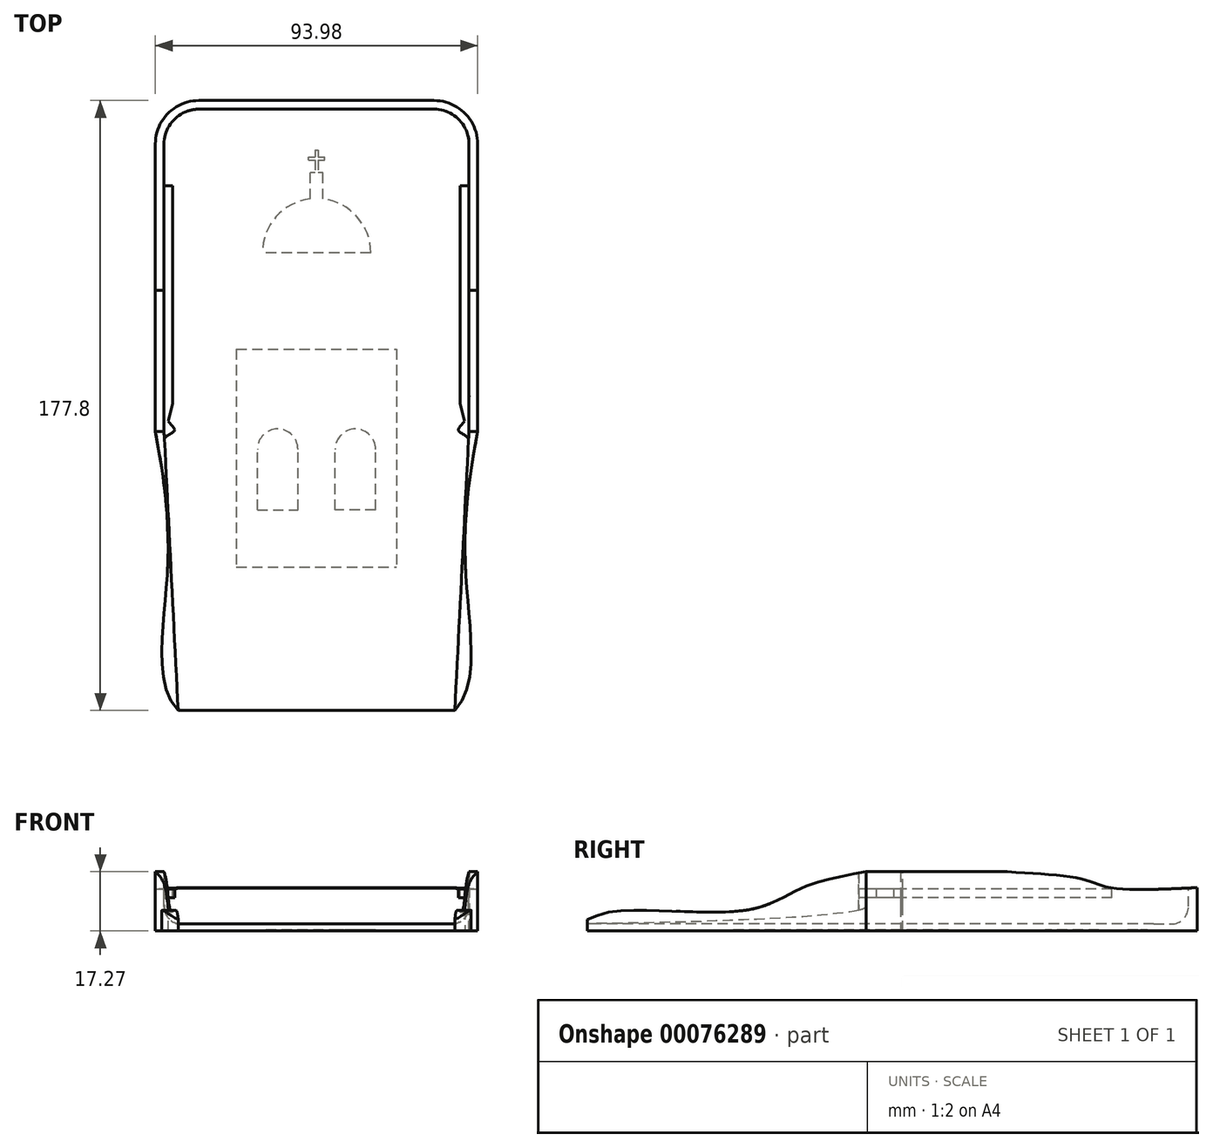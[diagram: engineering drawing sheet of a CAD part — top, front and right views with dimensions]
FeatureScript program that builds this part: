
annotation { "Feature Type Name" : "Feature", "Feature Type Description" : "" }
export const myFeature = defineFeature(function(context is Context, id is Id, definition is map)
    precondition{}
    {
        {
            var Q0;
            Q0=qCreatedBy(makeId("Top.planeOp"),FACE);
            var sketch = newSketch(context, id + "F0", { "sketchPlane" : qUnion([Q0])});
            skLineSegment(sketch, "E0.bottom", {"start": v(34.3, 88.9) * mm, "end": v(-34.3, 88.9) * mm});
            skLineSegment(sketch, "E0.top", {"start": v(46.99, -88.9) * mm, "end": v(-46.99, -88.9) * mm});
            skLineSegment(sketch, "E0.left", {"start": v(46.99, 76.2) * mm, "end": v(46.99, -88.9) * mm});
            skLineSegment(sketch, "E0.right", {"start": v(-47, 76.2) * mm, "end": v(-46.99, -88.9) * mm});
            skPoint(sketch, "E0.middle", {"position": v(0, 0) * mm});
            skPoint(sketch, "E1.visualSharp", {"position": v(-47, 88.9) * mm});
            skArc(sketch, "E1.filletArc", {"start": v(-34.3, 88.9) * mm, "mid": v(-43.27, 85.18) * mm, "end": v(-47, 76.2) * mm});
            skPoint(sketch, "E2.visualSharp", {"position": v(47, 88.9) * mm});
            skArc(sketch, "E2.filletArc", {"start": v(47, 76.2) * mm, "mid": v(43.27, 85.18) * mm, "end": v(34.3, 88.9) * mm});
            skLineSegment(sketch, "E3", {"start": v(0, -88.9) * mm, "end": v(-38.1, -88.9) * mm});
            skLineSegment(sketch, "E4", {"start": v(0, -88.9) * mm, "end": v(38.1, -88.9) * mm});
            skLineSegment(sketch, "E5", {"start": v(47, -88.9) * mm, "end": v(46.99, -7.62) * mm});
            skLineSegment(sketch, "E6.MirrorCS", {"start": v(-46.99, -88.9) * mm, "end": v(-47, -7.62) * mm});
            skPoint(sketch, "E7.1.internal.snap0", {"position": v(-46.99, -48.26) * mm});
            skFitSpline(sketch, "E7", {"points": [v(-46.99, -7.62) * mm, v(-43.45, -48.26) * mm, v(-40.33, -88.9) * mm, v(0, -95.06) * mm], "startDerivative": vector(20.85, -110.2) * mm, "endDerivative": vector(121.73, 3.89) * mm});
            skFitSpline(sketch, "E8.MirrorCS", {"points": [v(46.99, -7.62) * mm, v(43.45, -48.26) * mm, v(40.33, -88.9) * mm, v(0, -95.06) * mm], "startDerivative": vector(-20.85, -110.2) * mm, "endDerivative": vector(-121.73, 3.89) * mm});
            skLineSegment(sketch, "E9.bottom", {"start": v(-47, 66.55) * mm, "end": v(-44.45, 66.55) * mm});
            skLineSegment(sketch, "E9.left", {"start": v(-47, 66.55) * mm, "end": v(-46.99, -7.62) * mm});
            skLineSegment(sketch, "E10", {"start": v(53.05, 88.9) * mm, "end": v(-69.01, 88.9) * mm, "construction": true});
            skPoint(sketch, "E11.endSnap0", {"position": v(-46.99, 29.46) * mm});
            skLineSegment(sketch, "E12", {"start": v(-44.45, 66.55) * mm, "end": v(-44.45, 3.05) * mm});
            skLineSegment(sketch, "E13", {"start": v(-43.94, -2.03) * mm, "end": v(-43.94, -7.11) * mm});
            skPoint(sketch, "E14.1.internal.snap0", {"position": v(-43.94, -4.57) * mm});
            skLineSegment(sketch, "E15", {"start": v(0, 97.45) * mm, "end": v(0, -108.32) * mm, "construction": true});
            skLineSegment(sketch, "E16.MirrorCS", {"start": v(44.45, 66.55) * mm, "end": v(44.45, -2.03) * mm});
            skFitSpline(sketch, "E17.MirrorCS", {"points": [v(44.45, 3.05) * mm, v(42.16, -2.03) * mm], "startDerivative": vector(1.27, -5.08) * mm, "endDerivative": vector(1.27, -5.08) * mm});
            skFitSpline(sketch, "E18.MirrorCS", {"points": [v(42.16, -2.03) * mm, v(41, -4.57) * mm, v(42.16, -5.96) * mm, v(46.99, -7.62) * mm], "startDerivative": vector(-5.11, -7.46) * mm, "endDerivative": vector(3.51, -5.4) * mm});
            skSolve(sketch);
        }
        {
            var Q0;
            Q0=makeQuery(id+"F0.imprint","IMPRINT",FACE,{"disambiguationData":[TD([[makeQuery(id+"F0.imprint","IMPRINT",EDGE,{"derivedFrom":sQuery(id+"F0.wireOp",EDGE,"E0.bottom")}),1.0]])]});
            extrude(context, id + "F1", {"entities" : qUnion([Q0]), "depth" : 17.27 * mm});
        }
        {
            var Q0;
            Q0=makeQuery(id+"F1.opExtrude","CAP_FACE",FACE,{"disambiguationData":[OSD([sQuery(id+"F0.wireOp",EDGE,"E0.bottom"),sQuery(id+"F0.wireOp",EDGE,"E0.left"),sQuery(id+"F0.wireOp",EDGE,"E0.right"),sQuery(id+"F0.wireOp",EDGE,"E1.filletArc"),sQuery(id+"F0.wireOp",EDGE,"E2.filletArc"),sQuery(id+"F0.wireOp",EDGE,"E3"),sQuery(id+"F0.wireOp",EDGE,"E4"),sQuery(id+"F0.wireOp",EDGE,"E7"),sQuery(id+"F0.wireOp",EDGE,"E8.MirrorCS")])],"isStart":false});
            var sketch = newSketch(context, id + "F2", { "sketchPlane" : qUnion([Q0])});
            skLineSegment(sketch, "E19", {"start": v(-34.3, 86.36) * mm, "end": v(34.3, 86.36) * mm});
            skLineSegment(sketch, "E20", {"start": v(-44.45, 76.2) * mm, "end": v(-44.45, -7.62) * mm});
            skLineSegment(sketch, "E21", {"start": v(44.45, 76.2) * mm, "end": v(44.45, -7.62) * mm});
            skArc(sketch, "E22", {"start": v(-44.45, 76.2) * mm, "mid": v(-41.47, 83.38) * mm, "end": v(-34.3, 86.36) * mm});
            skArc(sketch, "E23", {"start": v(44.45, 76.2) * mm, "mid": v(41.47, 83.38) * mm, "end": v(34.3, 86.36) * mm});
            skLineSegment(sketch, "E24", {"start": v(-44.45, -7.62) * mm, "end": v(-44.45, -88.9) * mm, "construction": true});
            skLineSegment(sketch, "E25.MirrorCS", {"start": v(44.45, -7.62) * mm, "end": v(44.45, -88.9) * mm, "construction": true});
            skLineSegment(sketch, "E26", {"start": v(-44.45, -7.62) * mm, "end": v(-40.33, -88.9) * mm});
            skLineSegment(sketch, "E27.MirrorCS", {"start": v(44.45, -7.62) * mm, "end": v(40.33, -88.9) * mm});
            skLineSegment(sketch, "E28.bottom", {"start": v(-44.45, 64) * mm, "end": v(-41.91, 64) * mm});
            skLineSegment(sketch, "E28.top", {"start": v(-44.45, -4.57) * mm, "end": v(-41.9, -4.57) * mm});
            skLineSegment(sketch, "E28.left", {"start": v(-44.45, 64) * mm, "end": v(-44.45, -4.57) * mm});
            skLineSegment(sketch, "E28.right", {"start": v(-41.9, 64) * mm, "end": v(-41.9, -4.57) * mm});
            skLineSegment(sketch, "E29", {"start": v(48.82, 86.36) * mm, "end": v(-59.4, 86.36) * mm, "construction": true});
            skLineSegment(sketch, "E30", {"start": v(-35.18, 64) * mm, "end": v(-35.18, 0.5) * mm});
            skFitSpline(sketch, "E31", {"points": [v(-41.9, 0.5) * mm, v(-43.18, -4.57) * mm], "startDerivative": vector(-1.27, -5.08) * mm, "endDerivative": vector(-1.27, -5.08) * mm});
            skLineSegment(sketch, "E32", {"start": v(-44.97, -4.57) * mm, "end": v(-44.97, -9.65) * mm});
            skPoint(sketch, "E33.1.internal.snap0", {"position": v(-44.97, -7.11) * mm});
            skFitSpline(sketch, "E33", {"points": [v(-43.18, -4.57) * mm, v(-41.35, -7.11) * mm, v(-43.18, -8.6) * mm, v(-44.34, -9.7) * mm, v(-44.34, -9.8) * mm, v(-44.34, -9.8) * mm], "startDerivative": vector(5.13, -8.04) * mm, "endDerivative": vector(-0.1, 0.54) * mm});
            skLineSegment(sketch, "E34.MirrorCS", {"start": v(41.9, 64) * mm, "end": v(41.9, -4.57) * mm});
            skFitSpline(sketch, "E35.MirrorCS", {"points": [v(41.9, 0.5) * mm, v(43.18, -4.57) * mm], "startDerivative": vector(1.27, -5.08) * mm, "endDerivative": vector(1.27, -5.08) * mm});
            skFitSpline(sketch, "E36.MirrorCS", {"points": [v(43.18, -4.57) * mm, v(41.35, -7.11) * mm, v(43.18, -8.6) * mm, v(44.34, -9.7) * mm, v(44.34, -9.8) * mm, v(44.34, -9.8) * mm], "startDerivative": vector(-5.13, -8.04) * mm, "endDerivative": vector(0.1, 0.54) * mm});
            skLineSegment(sketch, "E37.MirrorCS", {"start": v(44.45, 64) * mm, "end": v(41.91, 64) * mm});
            skSolve(sketch);
        }
        {
            var Q0;
            Q0=makeQuery(id+"F2.imprint","IMPRINT",FACE,{"disambiguationData":[TD([[makeQuery(id+"F2.imprint","IMPRINT",EDGE,{"derivedFrom":sQuery(id+"F2.wireOp",EDGE,"E19")}),-1.0]])]});
            var Q1;
            {var subQ1=sQuery(id+"F2.wireOp",EDGE,"E28.bottom");Q1=makeQuery(id+"F2.imprint","IMPRINT",FACE,{"disambiguationData":[TD([[makeQuery(id+"F2.imprint","IMPRINT",EDGE,{"derivedFrom":subQ1}),-1.0]])]});}
            var Q2;
            {var subQ0=sQuery(id+"F2.wireOp",EDGE,"E26");var subQ1=sQuery(id+"F2.wireOp",EDGE,"E20");var subQ2=makeQuery(id+"F2.imprint","INTERSECT",VERTEX,{"derivedFrom":[subQ1,subQ0]});Q2=makeQuery(id+"F2.imprint","IMPRINT",FACE,{"disambiguationData":[TD([[makeQuery(id+"F2.imprint","IMPRINT",EDGE,{"disambiguationData":[TD([[subQ2,-1.0]])],"derivedFrom":subQ0}),1.0]])]});}
            var Q3;
            {var subQ3=sQuery(id+"F2.wireOp",EDGE,"E31");Q3=makeQuery(id+"F2.imprint","IMPRINT",FACE,{"disambiguationData":[TD([[makeQuery(id+"F2.imprint","IMPRINT",EDGE,{"derivedFrom":subQ3}),1.0]])]});}
            var Q4;
            {var subQ2=sQuery(id+"F2.wireOp",EDGE,"E35.MirrorCS");Q4=makeQuery(id+"F2.imprint","IMPRINT",FACE,{"disambiguationData":[TD([[makeQuery(id+"F2.imprint","IMPRINT",EDGE,{"derivedFrom":subQ2}),1.0]])]});}
            extrude(context, id + "F3", {"entities" : qUnion([Q0, Q1, Q2, Q3, Q4]), "operationType" : NewBodyOperationType.REMOVE, "oppositeDirection" : true, "depth" : 15.24 * mm});
        }
        {
            var Q0;
            Q0=makeQuery(id+"F1.opExtrude","SWEPT_FACE",FACE,{"disambiguationData":[OSD([sQuery(id+"F0.wireOp",EDGE,"E0.left")])]});
            var sketch = newSketch(context, id + "F4", { "sketchPlane" : qUnion([Q0])});
            skLineSegment(sketch, "E38", {"start": v(-90.42, 3.23) * mm, "end": v(-90.42, 2.54) * mm});
            skLineSegment(sketch, "E39", {"start": v(-90.42, 2.54) * mm, "end": v(-7.62, 2.54) * mm});
            skLineSegment(sketch, "E40", {"start": v(-90.42, 2.54) * mm, "end": v(-90.42, 0) * mm});
            skLineSegment(sketch, "E41", {"start": v(-7.62, 2.54) * mm, "end": v(-7.62, 17.27) * mm});
            skFitSpline(sketch, "E42", {"points": [v(-7.62, 17.27) * mm, v(-25.99, 12.69) * mm, v(-41.86, 6.2) * mm, v(-79.71, 5.87) * mm, v(-90.42, 2.54) * mm], "startDerivative": vector(-81.4, -14.51) * mm, "endDerivative": vector(-44.44, -23.04) * mm});
            skLineSegment(sketch, "E43", {"start": v(-7.62, 17.27) * mm, "end": v(-90.42, 17.27) * mm});
            skLineSegment(sketch, "E44", {"start": v(-90.42, 17.27) * mm, "end": v(-90.42, 3.23) * mm});
            skLineSegment(sketch, "E45", {"start": v(90.03, 0) * mm, "end": v(90.03, 12.7) * mm});
            skLineSegment(sketch, "E46", {"start": v(90.03, 12.7) * mm, "end": v(90.06, 17.27) * mm});
            skPoint(sketch, "E47.1.internal.snap0", {"position": v(90.04, 14.99) * mm});
            skFitSpline(sketch, "E47", {"points": [v(33.54, 17.27) * mm, v(55.9, 14.99) * mm, v(63.11, 12.7) * mm, v(90.03, 12.7) * mm], "startDerivative": vector(70.29, -4.08) * mm, "endDerivative": vector(78.4, 3.83) * mm});
            skLineSegment(sketch, "E48", {"start": v(33.54, 17.27) * mm, "end": v(90.06, 17.27) * mm});
            skSolve(sketch);
        }
        {
            var Q0;
            Q0=makeQuery(id+"F4.imprint","IMPRINT",FACE,{"disambiguationData":[TD([[makeQuery(id+"F4.imprint","IMPRINT",EDGE,{"derivedFrom":sQuery(id+"F4.wireOp",EDGE,"E38")}),1.0]])]});
            extrude(context, id + "F5", {"entities" : qUnion([Q0]), "operationType" : NewBodyOperationType.REMOVE, "oppositeDirection" : true, "depth" : 101.6 * mm});
        }
        {
            var Q0;
            {var subQ0=sQuery(id+"F4.wireOp",EDGE,"E48");var subQ1=sQuery(id+"F4.wireOp",EDGE,"E47");var subQ2=sQuery(id+"F0.wireOp",EDGE,"E0.left");var subQ3=makeQuery(id+"F4.imprint","INTERSECT",VERTEX,{"derivedFrom":[makeQuery(id+"F1.opExtrude","CAP_EDGE",EDGE,{"disambiguationData":[OSD([subQ2])],"isStart":false}),subQ1,subQ0]});Q0=makeQuery(id+"F4.imprint","IMPRINT",FACE,{"disambiguationData":[TD([[makeQuery(id+"F4.imprint","IMPRINT",EDGE,{"disambiguationData":[TD([[subQ3,-1.0]])],"derivedFrom":subQ1}),1.0]])]});}
            var Q1;
            {var subQ0=sQuery(id+"F4.wireOp",EDGE,"E46");Q1=makeQuery(id+"F4.imprint","IMPRINT",FACE,{"disambiguationData":[TD([[makeQuery(id+"F4.imprint","IMPRINT",EDGE,{"derivedFrom":subQ0}),1.0]])]});}
            extrude(context, id + "F6", {"entities" : qUnion([Q0, Q1]), "operationType" : NewBodyOperationType.REMOVE, "oppositeDirection" : true, "depth" : 101.6 * mm});
        }
        {
            var Q0;
            {var subQ1=sQuery(id+"F2.wireOp",EDGE,"E28.bottom");Q0=makeQuery(id+"F2.imprint","IMPRINT",FACE,{"disambiguationData":[TD([[makeQuery(id+"F2.imprint","IMPRINT",EDGE,{"derivedFrom":subQ1}),-1.0]])]});}
            var Q1;
            {var subQ0=sQuery(id+"F2.wireOp",EDGE,"E26");var subQ1=sQuery(id+"F2.wireOp",EDGE,"E20");var subQ2=makeQuery(id+"F2.imprint","INTERSECT",VERTEX,{"derivedFrom":[subQ1,subQ0]});Q1=makeQuery(id+"F2.imprint","IMPRINT",FACE,{"disambiguationData":[TD([[makeQuery(id+"F2.imprint","IMPRINT",EDGE,{"disambiguationData":[TD([[subQ2,-1.0]])],"derivedFrom":subQ0}),1.0]])]});}
            var Q2;
            {var subQ2=sQuery(id+"F2.wireOp",EDGE,"E35.MirrorCS");Q2=makeQuery(id+"F2.imprint","IMPRINT",FACE,{"disambiguationData":[TD([[makeQuery(id+"F2.imprint","IMPRINT",EDGE,{"derivedFrom":subQ2}),1.0]])]});}
            extrude(context, id + "F7", {"entities" : qUnion([Q0, Q1, Q2]), "operationType" : NewBodyOperationType.ADD, "oppositeDirection" : true, "depth" : 7.62 * mm, "hasSecondDirection" : true, "secondDirectionOppositeDirection" : true, "secondDirectionDepth" : 5.08 * mm});
        }
        {
            var Q0;
            Q0=makeQuery(id+"F1.opExtrude","CAP_FACE",FACE,{"disambiguationData":[OSD([sQuery(id+"F0.wireOp",EDGE,"E0.bottom"),sQuery(id+"F0.wireOp",EDGE,"E0.left"),sQuery(id+"F0.wireOp",EDGE,"E0.right"),sQuery(id+"F0.wireOp",EDGE,"E1.filletArc"),sQuery(id+"F0.wireOp",EDGE,"E2.filletArc"),sQuery(id+"F0.wireOp",EDGE,"E3"),sQuery(id+"F0.wireOp",EDGE,"E4"),sQuery(id+"F0.wireOp",EDGE,"E7"),sQuery(id+"F0.wireOp",EDGE,"E8.MirrorCS"),sQuery(id+"F0.wireOp",EDGE,"E9.left"),sQuery(id+"F0.wireOp",EDGE,"E16.MirrorCS"),sQuery(id+"F0.wireOp",EDGE,"E17.MirrorCS")])],"isStart":true});
            var sketch = newSketch(context, id + "F8", { "sketchPlane" : qUnion([Q0])});
            skLineSegment(sketch, "E49.bottom", {"start": v(-23.35, -16.42) * mm, "end": v(23.35, -16.42) * mm});
            skLineSegment(sketch, "E49.top", {"start": v(-23.35, 47.08) * mm, "end": v(23.35, 47.08) * mm});
            skLineSegment(sketch, "E49.left", {"start": v(-23.35, -16.42) * mm, "end": v(-23.35, 47.08) * mm});
            skLineSegment(sketch, "E49.right", {"start": v(23.35, -16.42) * mm, "end": v(23.35, 47.08) * mm});
            skPoint(sketch, "E49.middle", {"position": v(0, 15.33) * mm});
            skLineSegment(sketch, "E50.bottom", {"start": v(15.85, -16.42) * mm, "end": v(-15.79, -16.42) * mm});
            skLineSegment(sketch, "E50.top", {"start": v(15.85, -44.5) * mm, "end": v(-15.79, -44.5) * mm});
            skLineSegment(sketch, "E50.left", {"start": v(15.85, -16.42) * mm, "end": v(15.85, -44.5) * mm});
            skLineSegment(sketch, "E50.right", {"start": v(-15.79, -16.42) * mm, "end": v(-15.79, -44.5) * mm});
            skArc(sketch, "E51", {"start": v(-15.79, -44.5) * mm, "mid": v(0.03, -60.32) * mm, "end": v(15.85, -44.5) * mm});
            skLineSegment(sketch, "E52.bottom", {"start": v(-1.84, -52.63) * mm, "end": v(1.84, -52.63) * mm});
            skLineSegment(sketch, "E52.top", {"start": v(-1.84, -68.01) * mm, "end": v(1.84, -68.01) * mm});
            skLineSegment(sketch, "E52.left", {"start": v(-1.84, -52.63) * mm, "end": v(-1.84, -68.01) * mm});
            skLineSegment(sketch, "E52.right", {"start": v(1.84, -52.63) * mm, "end": v(1.84, -68.01) * mm});
            skPoint(sketch, "E52.middle", {"position": v(0, -60.32) * mm});
            skPoint(sketch, "E52.middle.positionSnap0", {"position": v(0.03, -60.32) * mm});
            skPoint(sketch, "E52.centerSnap0", {"position": v(0.03, -60.32) * mm});
            skLineSegment(sketch, "E53.bottom", {"start": v(-0.44, -74.46) * mm, "end": v(0.44, -74.46) * mm});
            skLineSegment(sketch, "E53.top", {"start": v(-0.44, -61.56) * mm, "end": v(0.44, -61.56) * mm});
            skLineSegment(sketch, "E53.left", {"start": v(-0.44, -74.46) * mm, "end": v(-0.44, -61.56) * mm});
            skLineSegment(sketch, "E53.right", {"start": v(0.44, -74.46) * mm, "end": v(0.44, -61.56) * mm});
            skPoint(sketch, "E53.middle", {"position": v(0, -68.01) * mm});
            skLineSegment(sketch, "E54.bottom", {"start": v(-2.35, -71.57) * mm, "end": v(2.35, -71.57) * mm});
            skLineSegment(sketch, "E54.top", {"start": v(-2.35, -72.41) * mm, "end": v(2.35, -72.41) * mm});
            skLineSegment(sketch, "E54.left", {"start": v(-2.35, -71.57) * mm, "end": v(-2.35, -72.41) * mm});
            skLineSegment(sketch, "E54.right", {"start": v(2.35, -71.57) * mm, "end": v(2.35, -72.41) * mm});
            skPoint(sketch, "E54.middle", {"position": v(0, -72) * mm});
            skLineSegment(sketch, "E55.bottom", {"start": v(11.96, -21.87) * mm, "end": v(3.03, -21.87) * mm});
            skLineSegment(sketch, "E55.top", {"start": v(11.96, -32.71) * mm, "end": v(3.03, -32.71) * mm});
            skLineSegment(sketch, "E55.left", {"start": v(11.96, -21.87) * mm, "end": v(11.96, -32.71) * mm});
            skLineSegment(sketch, "E55.right", {"start": v(3.03, -21.87) * mm, "end": v(3.03, -32.71) * mm});
            skArc(sketch, "E56", {"start": v(3.03, -32.71) * mm, "mid": v(7.5, -37.18) * mm, "end": v(11.96, -32.71) * mm});
            skLineSegment(sketch, "E57.MirrorCS", {"start": v(-3.03, -21.87) * mm, "end": v(-3.03, -32.71) * mm});
            skLineSegment(sketch, "E58.MirrorCS", {"start": v(-11.96, -32.71) * mm, "end": v(-3.03, -32.71) * mm});
            skArc(sketch, "E59.MirrorCS", {"start": v(-3.03, -32.71) * mm, "mid": v(-7.5, -37.18) * mm, "end": v(-11.96, -32.71) * mm});
            skLineSegment(sketch, "E60.MirrorCS", {"start": v(-11.96, -21.87) * mm, "end": v(-11.96, -32.71) * mm});
            skLineSegment(sketch, "E61.MirrorCS", {"start": v(-11.96, -21.87) * mm, "end": v(-3.03, -21.87) * mm});
            skLineSegment(sketch, "E62.bottom", {"start": v(17.22, 30.43) * mm, "end": v(5.42, 30.43) * mm});
            skLineSegment(sketch, "E62.top", {"start": v(17.22, 12.73) * mm, "end": v(5.42, 12.73) * mm});
            skLineSegment(sketch, "E62.left", {"start": v(17.22, 30.43) * mm, "end": v(17.22, 12.73) * mm});
            skLineSegment(sketch, "E62.right", {"start": v(5.42, 30.43) * mm, "end": v(5.42, 12.73) * mm});
            skArc(sketch, "E63", {"start": v(5.42, 12.73) * mm, "mid": v(11.32, 6.83) * mm, "end": v(17.22, 12.73) * mm});
            skArc(sketch, "E64.MirrorCS", {"start": v(-5.42, 12.73) * mm, "mid": v(-11.32, 6.83) * mm, "end": v(-17.22, 12.73) * mm});
            skLineSegment(sketch, "E65.MirrorCS", {"start": v(-17.22, 12.73) * mm, "end": v(-5.42, 12.73) * mm});
            skLineSegment(sketch, "E66.MirrorCS", {"start": v(-5.42, 30.43) * mm, "end": v(-5.42, 12.73) * mm});
            skLineSegment(sketch, "E67.MirrorCS", {"start": v(-17.22, 30.43) * mm, "end": v(-5.42, 30.43) * mm});
            skLineSegment(sketch, "E68.MirrorCS", {"start": v(-17.22, 30.43) * mm, "end": v(-17.22, 12.73) * mm});
            skSolve(sketch);
        }
        {
            var Q0;
            Q0=makeQuery(id+"F8.imprint","IMPRINT",FACE,{"disambiguationData":[TD([[makeQuery(id+"F8.imprint","IMPRINT",EDGE,{"derivedFrom":sQuery(id+"F8.wireOp",EDGE,"E49.top")}),-1.0]])]});
            var Q1;
            Q1=makeQuery(id+"F8.imprint","IMPRINT",FACE,{"disambiguationData":[TD([[makeQuery(id+"F8.imprint","IMPRINT",EDGE,{"derivedFrom":sQuery(id+"F8.wireOp",EDGE,"E50.bottom")}),1.0]])]});
            var Q2;
            {var subQ2=sQuery(id+"F8.wireOp",EDGE,"E50.top");Q2=makeQuery(id+"F8.imprint","IMPRINT",FACE,{"disambiguationData":[TD([[makeQuery(id+"F8.imprint","IMPRINT",EDGE,{"derivedFrom":subQ2}),1.0]])]});}
            var Q3;
            {var subQ5=sQuery(id+"F8.wireOp",EDGE,"E52.bottom");Q3=makeQuery(id+"F8.imprint","IMPRINT",FACE,{"disambiguationData":[TD([[makeQuery(id+"F8.imprint","IMPRINT",EDGE,{"derivedFrom":subQ5}),-1.0]])]});}
            var Q4;
            {var subQ11=sQuery(id+"F8.wireOp",EDGE,"E53.top");Q4=makeQuery(id+"F8.imprint","IMPRINT",FACE,{"disambiguationData":[TD([[makeQuery(id+"F8.imprint","IMPRINT",EDGE,{"derivedFrom":subQ11}),1.0]])]});}
            var Q5;
            {var subQ5=sQuery(id+"F8.wireOp",EDGE,"E53.top");Q5=makeQuery(id+"F8.imprint","IMPRINT",FACE,{"disambiguationData":[TD([[makeQuery(id+"F8.imprint","IMPRINT",EDGE,{"derivedFrom":subQ5}),-1.0]])]});}
            var Q6;
            {var subQ0=sQuery(id+"F8.wireOp",EDGE,"E53.bottom");Q6=makeQuery(id+"F8.imprint","IMPRINT",FACE,{"disambiguationData":[TD([[makeQuery(id+"F8.imprint","IMPRINT",EDGE,{"derivedFrom":subQ0}),1.0]])]});}
            var Q7;
            {var subQ0=sQuery(id+"F8.wireOp",EDGE,"E53.left");var subQ1=sQuery(id+"F8.wireOp",EDGE,"E52.top");var subQ2=makeQuery(id+"F8.imprint","INTERSECT",VERTEX,{"derivedFrom":[subQ1,subQ0]});Q7=makeQuery(id+"F8.imprint","IMPRINT",FACE,{"disambiguationData":[TD([[makeQuery(id+"F8.imprint","IMPRINT",EDGE,{"disambiguationData":[TD([[subQ2,-1.0]])],"derivedFrom":subQ1}),-1.0]])]});}
            var Q8;
            {var subQ5=sQuery(id+"F8.wireOp",EDGE,"E54.right");Q8=makeQuery(id+"F8.imprint","IMPRINT",FACE,{"disambiguationData":[TD([[makeQuery(id+"F8.imprint","IMPRINT",EDGE,{"derivedFrom":subQ5}),-1.0]])]});}
            var Q9;
            {var subQ5=sQuery(id+"F8.wireOp",EDGE,"E54.left");Q9=makeQuery(id+"F8.imprint","IMPRINT",FACE,{"disambiguationData":[TD([[makeQuery(id+"F8.imprint","IMPRINT",EDGE,{"derivedFrom":subQ5}),1.0]])]});}
            var Q10;
            {var subQ0=sQuery(id+"F8.wireOp",EDGE,"E54.top");var subQ1=sQuery(id+"F8.wireOp",EDGE,"E53.left");var subQ2=makeQuery(id+"F8.imprint","INTERSECT",VERTEX,{"derivedFrom":[subQ1,subQ0]});Q10=makeQuery(id+"F8.imprint","IMPRINT",FACE,{"disambiguationData":[TD([[makeQuery(id+"F8.imprint","IMPRINT",EDGE,{"disambiguationData":[TD([[subQ2,-1.0]])],"derivedFrom":subQ1}),-1.0]])]});}
            extrude(context, id + "F9", {"entities" : qUnion([Q0, Q1, Q2, Q3, Q4, Q5, Q6, Q7, Q8, Q9, Q10]), "operationType" : NewBodyOperationType.REMOVE, "oppositeDirection" : true, "depth" : 0.25 * mm});
        }
        {
            var Q0;
            Q0=makeQuery(id+"F3.boolean.opBoolean","COPY",EDGE,{"derivedFrom":makeQuery(id+"F3.opExtrude","CAP_EDGE",EDGE,{"disambiguationData":[OSD([sQuery(id+"F2.wireOp",EDGE,"E22")])],"isStart":false})});
            fillet(context, id + "F10", {"entities" : qUnion([Q0]), "radius" : 5.08 * mm, "tangentPropagation" : true, "allowEdgeOverflow" : false});
        }
    });
